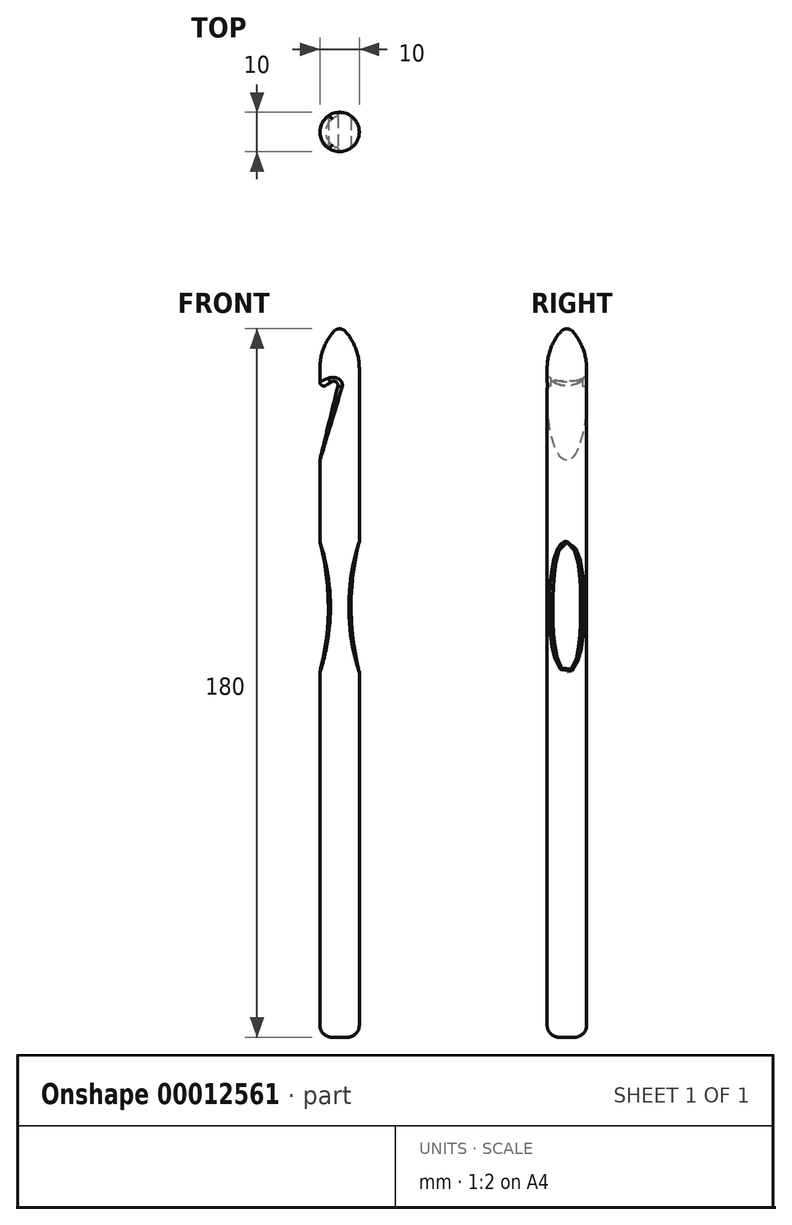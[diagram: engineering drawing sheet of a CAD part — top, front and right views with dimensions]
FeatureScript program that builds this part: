
annotation { "Feature Type Name" : "Feature", "Feature Type Description" : "" }
export const myFeature = defineFeature(function(context is Context, id is Id, definition is map)
    precondition{}
    {
        {
            var Q0;
            Q0=qCreatedBy(makeId("Front.planeOp"),FACE);
            var sketch = newSketch(context, id + "F0", { "sketchPlane" : qUnion([Q0])});
            skLineSegment(sketch, "E0", {"start": v(0, 0) * mm, "end": v(5, 0) * mm});
            skLineSegment(sketch, "E1", {"start": v(5, 0) * mm, "end": v(5, 170) * mm});
            skLineSegment(sketch, "E2", {"start": v(0, 0) * mm, "end": v(0, 180) * mm});
            skLineSegment(sketch, "E3", {"start": v(0, 180) * mm, "end": v(5, 180) * mm, "construction": true});
            skLineSegment(sketch, "E4", {"start": v(5, 180) * mm, "end": v(5, 170) * mm, "construction": true});
            skArc(sketch, "E5", {"start": v(1.5, 179.32) * mm, "mid": v(0.83, 179.82) * mm, "end": v(0, 180) * mm});
            skArc(sketch, "E6", {"start": v(5, 170) * mm, "mid": v(4.1, 174.97) * mm, "end": v(1.5, 179.32) * mm});
            skSolve(sketch);
        }
        {
            var Q0;
            Q0 = qSketchRegion(id + "F0", true);
            var Q1;
            Q1=sQuery(id+"F0.wireOp",EDGE,"E2");
            revolve(context, id + "F1", {"entities" : qUnion([Q0]), "axis" : qUnion([Q1]), "revolveType" : RevolveType.FULL});
        }
        {
            var Q0;
            Q0=qCreatedBy(makeId("Front.planeOp"),FACE);
            var sketch = newSketch(context, id + "F2", { "sketchPlane" : qUnion([Q0])});
            skLineSegment(sketch, "E7", {"start": v(0, 0) * mm, "end": v(0, 179.32) * mm, "construction": true});
            skLineSegment(sketch, "E8", {"start": v(-8, 159.32) * mm, "end": v(-8, 134.32) * mm});
            skLineSegment(sketch, "E9", {"start": v(-8, 134.32) * mm, "end": v(0, 167.32) * mm});
            skLineSegment(sketch, "E10", {"start": v(0, 167.32) * mm, "end": v(-8, 159.32) * mm, "construction": true});
            skArc(sketch, "E11", {"start": v(0, 167.32) * mm, "mid": v(-5, 164.32) * mm, "end": v(-8, 159.32) * mm});
            skSolve(sketch);
        }
        {
            var Q0;
            Q0 = qSketchRegion(id + "F2", true);
            extrude(context, id + "F3", {"entities" : qUnion([Q0]), "operationType" : NewBodyOperationType.REMOVE, "oppositeDirection" : true, "depth" : 25 * mm, "hasSecondDirection" : true, "secondDirectionOppositeDirection" : false, "secondDirectionDepth" : 25 * mm});
        }
        {
            var Q0;
            Q0=qCreatedBy(makeId("Front.planeOp"),FACE);
            var sketch = newSketch(context, id + "F4", { "sketchPlane" : qUnion([Q0])});
            skLineSegment(sketch, "E12", {"start": v(-6, 129.32) * mm, "end": v(-6, 89.32) * mm});
            skLineSegment(sketch, "E13", {"start": v(-6, 89.32) * mm, "end": v(6, 89.32) * mm, "construction": true});
            skLineSegment(sketch, "E14", {"start": v(6, 89.32) * mm, "end": v(6, 129.32) * mm});
            skLineSegment(sketch, "E15", {"start": v(6, 129.32) * mm, "end": v(-6, 129.32) * mm, "construction": true});
            skLineSegment(sketch, "E16", {"start": v(0, 0) * mm, "end": v(0, 179.32) * mm, "construction": true});
            skArc(sketch, "E17", {"start": v(-6, 89.32) * mm, "mid": v(-2.87, 109.32) * mm, "end": v(-6, 129.32) * mm});
            skArc(sketch, "E18", {"start": v(6, 129.32) * mm, "mid": v(2.87, 109.32) * mm, "end": v(6, 89.32) * mm});
            skSolve(sketch);
        }
        {
            var Q0;
            Q0 = qSketchRegion(id + "F4", true);
            extrude(context, id + "F5", {"entities" : qUnion([Q0]), "operationType" : NewBodyOperationType.REMOVE, "oppositeDirection" : true, "depth" : 25 * mm, "hasSecondDirection" : true, "secondDirectionOppositeDirection" : false, "secondDirectionDepth" : 25 * mm});
        }
        {
            var Q0;
            Q0=makeQuery(id+"F3.boolean.opBoolean","COPY",EDGE,{"derivedFrom":makeQuery(id+"F3.opExtrude","SWEPT_EDGE",EDGE,{"disambiguationData":[OSD([sQuery(id+"F2.wireOp",EDGE,"E9"),sQuery(id+"F2.wireOp",EDGE,"E11")])]})});
            fillet(context, id + "F6", {"entities" : qUnion([Q0]), "radius" : 1 * mm, "tangentPropagation" : true, "allowEdgeOverflow" : false});
        }
        {
            var Q0;
            Q0=makeQuery(id+"F3.boolean.opBoolean","INTERSECT",EDGE,{"derivedFrom":[makeQuery(id+"F1.opRevolve","SWEPT_FACE",FACE,{"disambiguationData":[OSD([sQuery(id+"F0.wireOp",EDGE,"E1")])]}),makeQuery(id+"F3.opExtrude","SWEPT_FACE",FACE,{"disambiguationData":[OSD([sQuery(id+"F2.wireOp",EDGE,"E11")])]})]});
            var Q1;
            Q1=makeQuery(id+"F6.opFillet","BLEND_EDGE",EDGE,{"disambiguationData":[OD(1.0)],"blendedFrom":[makeQuery(id+"F3.boolean.opBoolean","COPY",EDGE,{"derivedFrom":makeQuery(id+"F3.opExtrude","SWEPT_EDGE",EDGE,{"disambiguationData":[OSD([sQuery(id+"F2.wireOp",EDGE,"E9"),sQuery(id+"F2.wireOp",EDGE,"E11")])]})}),makeQuery(id+"F1.opRevolve","SWEPT_FACE",FACE,{"disambiguationData":[OSD([sQuery(id+"F0.wireOp",EDGE,"E1")])]})],"blendedInto":[makeQuery(id+"F1.opRevolve","SWEPT_FACE",FACE,{"disambiguationData":[OSD([sQuery(id+"F0.wireOp",EDGE,"E1")])]})]});
            var Q2;
            Q2=makeQuery(id+"F3.boolean.opBoolean","INTERSECT",EDGE,{"derivedFrom":[makeQuery(id+"F1.opRevolve","SWEPT_FACE",FACE,{"disambiguationData":[OSD([sQuery(id+"F0.wireOp",EDGE,"E1")])]}),makeQuery(id+"F3.opExtrude","SWEPT_FACE",FACE,{"disambiguationData":[OSD([sQuery(id+"F2.wireOp",EDGE,"E9")])]})]});
            var Q3;
            Q3=makeQuery(id+"F6.opFillet","BLEND_EDGE",EDGE,{"disambiguationData":[OD(0.0)],"blendedFrom":[makeQuery(id+"F3.boolean.opBoolean","COPY",EDGE,{"derivedFrom":makeQuery(id+"F3.opExtrude","SWEPT_EDGE",EDGE,{"disambiguationData":[OSD([sQuery(id+"F2.wireOp",EDGE,"E9"),sQuery(id+"F2.wireOp",EDGE,"E11")])]})}),makeQuery(id+"F1.opRevolve","SWEPT_FACE",FACE,{"disambiguationData":[OSD([sQuery(id+"F0.wireOp",EDGE,"E1")])]})],"blendedInto":[makeQuery(id+"F1.opRevolve","SWEPT_FACE",FACE,{"disambiguationData":[OSD([sQuery(id+"F0.wireOp",EDGE,"E1")])]})]});
            fillet(context, id + "F7", {"entities" : qUnion([Q0, Q1, Q2, Q3]), "radius" : 1 * mm, "tangentPropagation" : true, "allowEdgeOverflow" : false});
        }
        {
            var Q0;
            Q0=makeQuery(id+"F5.boolean.opBoolean","INTERSECT",EDGE,{"derivedFrom":[makeQuery(id+"F1.opRevolve","SWEPT_FACE",FACE,{"disambiguationData":[OSD([sQuery(id+"F0.wireOp",EDGE,"E1")])]}),makeQuery(id+"F5.opExtrude","SWEPT_FACE",FACE,{"disambiguationData":[OSD([sQuery(id+"F4.wireOp",EDGE,"E17")])]})]});
            var Q1;
            Q1=makeQuery(id+"F5.boolean.opBoolean","INTERSECT",EDGE,{"derivedFrom":[makeQuery(id+"F1.opRevolve","SWEPT_FACE",FACE,{"disambiguationData":[OSD([sQuery(id+"F0.wireOp",EDGE,"E1")])]}),makeQuery(id+"F5.opExtrude","SWEPT_FACE",FACE,{"disambiguationData":[OSD([sQuery(id+"F4.wireOp",EDGE,"E18")])]})]});
            fillet(context, id + "F8", {"entities" : qUnion([Q0, Q1]), "radius" : 1 * mm, "tangentPropagation" : true, "allowEdgeOverflow" : false});
        }
        {
            var Q0;
            Q0=makeQuery(id+"F1.opRevolve","SWEPT_EDGE",EDGE,{"disambiguationData":[OSD([sQuery(id+"F0.wireOp",EDGE,"E0"),sQuery(id+"F0.wireOp",EDGE,"E1")])]});
            fillet(context, id + "F9", {"entities" : qUnion([Q0]), "radius" : 3 * mm, "tangentPropagation" : true, "allowEdgeOverflow" : false});
        }
    });
